# Revit family: Difusores de chorro_Aguilera Extincion
name_source: partatom
category: Rociadores
revit_build: Autodesk Revit 2017 (Build: 20160225_1515(x64)
units: mm (PartAtom-declared; Revit-internal decimal feet)

## family parameters
Compartido = No
Corte con vacíos al cargar = No
Cota de conector redondo = Radio de uso
Mantener orientación de anotación = No
Número OmniClass = 23.65.70.17.11.24
Punto de cálculo de habitación = No
Se basa en plano de trabajo = Sí
Siempre vertical = Sí
Tipo de pieza = Normal
Título OmniClass = Fire Fighting Sprinkler Heads

## types (7) — shared parameters
Clase de presión = Norma
Cobertura = Norma
Descripción = Componente que permite obtener un caudal predeterminado y una característica de distribución uniforme del agente extintor dentro o sobre el riesgo protegido.
Diámetro = 6 mm
Fabricante = Aguilera Extinción
Orificio = Norma
Respuesta = Norma
Símbolo = Sí
Símbolo texto modelo = Sí
URL = http://aguilera.es
Zona de acción = Sí
zero-valued in all types: Elevación por defecto

## per-type parameters (varying)
| type | Altura | Dd | Hexagonal | Hr | Modelo | Radio | Rh | Rosca |
| Difusor de chorro 1/4" hembra | 30 mm  [stored 0.0984252 ft] | 5 mm  [stored 0.0164042 ft] | 18 mm  [stored 0.0590551 ft] | 9 mm  [stored 0.0295276 ft] | AEX/DCH14 | 3 mm | 9 mm  [stored 0.0295276 ft] | 6 mm |
| Difusor de chorro 3/8" hembra | 35 mm  [stored 0.114829 ft] | 6 mm  [stored 0.019685 ft] | 22 mm  [stored 0.0721785 ft] | 10 mm  [stored 0.0328084 ft] | AEX/DCH38 | 5 mm | 11 mm  [stored 0.0360892 ft] | 10 mm |
| Difusor de chorro 1/2" hembra | 46 mm  [stored 0.150919 ft] | 8 mm  [stored 0.0262467 ft] | 27 mm  [stored 0.0885827 ft] | 13 mm | AEX/DCH12 | 6 mm | 14 mm  [stored 0.0459318 ft] | 13 mm |
| Difusor de chorro 3/4" hembra | 50 mm  [stored 0.164042 ft] | 8 mm  [stored 0.0262467 ft] | 32 mm  [stored 0.104987 ft] | 14 mm  [stored 0.0459318 ft] | AEX/DCH34 | 10 mm | 16 mm  [stored 0.0524934 ft] | 19 mm |
| Difusor de chorro 1" hembra | 60 mm  [stored 0.19685 ft] | 10 mm  [stored 0.0328084 ft] | 40 mm  [stored 0.131234 ft] | 17 mm | AEX/DCH1 | 13 mm | 20 mm  [stored 0.0656168 ft] | 25 mm |
| Difusor de chorro 1 1/4" hembra | 70 mm  [stored 0.229659 ft] | 12 mm  [stored 0.0393701 ft] | 50 mm  [stored 0.164042 ft] | 20 mm  [stored 0.0656168 ft] | AEX/DCH114 | 16 mm | 25 mm  [stored 0.082021 ft] | 32 mm |
| Difusor de chorro 1 1/2" hembra | 85 mm  [stored 0.278871 ft] | 14 mm  [stored 0.0459318 ft] | 60 mm  [stored 0.19685 ft] | 24 mm  [stored 0.0787402 ft] | AEX/DCH112 | 19 mm | 30 mm  [stored 0.0984252 ft] | 38 mm |

note: [stored X ft] marks values corroborated as IEEE doubles in the binary element streams (Revit-internal decimal feet)
